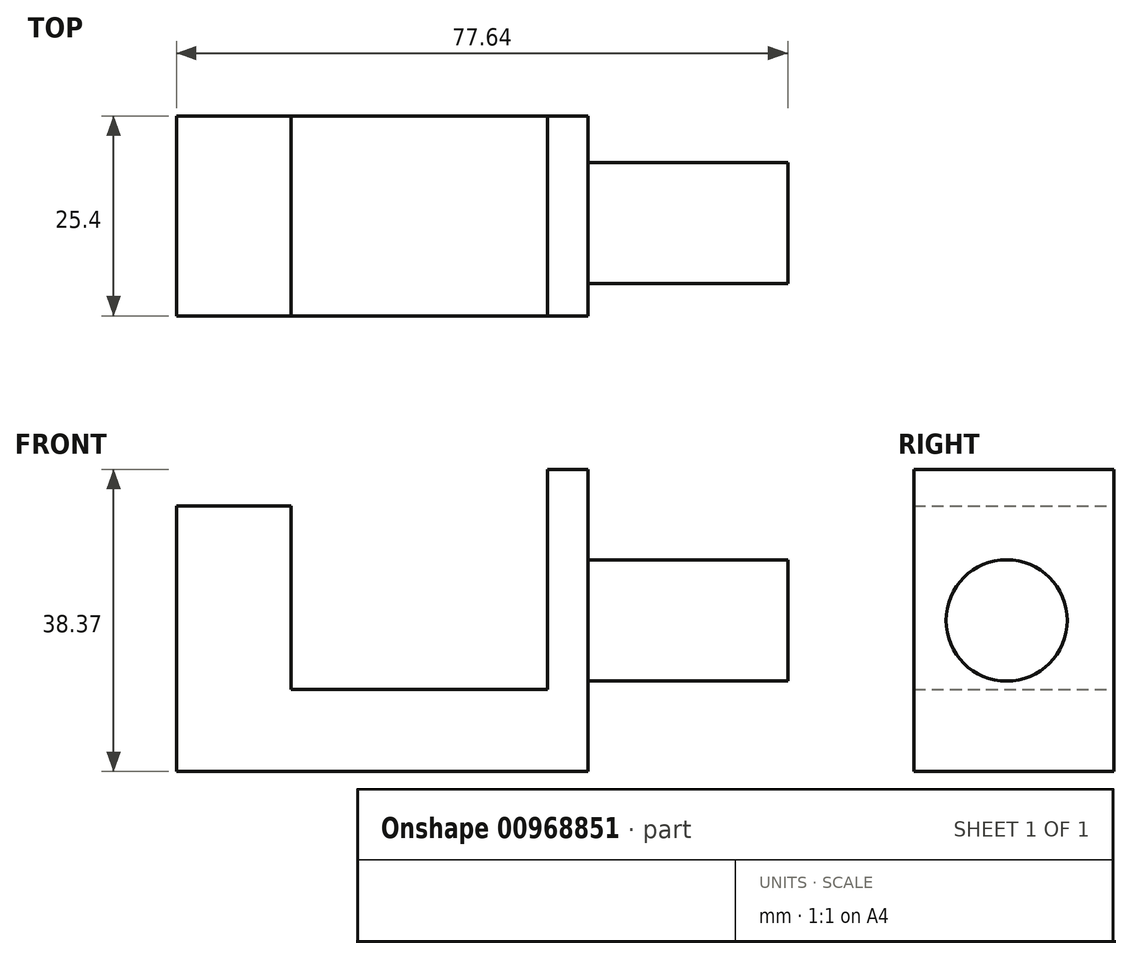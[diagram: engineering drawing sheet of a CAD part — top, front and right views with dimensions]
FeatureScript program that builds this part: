
annotation { "Feature Type Name" : "Feature", "Feature Type Description" : "" }
export const myFeature = defineFeature(function(context is Context, id is Id, definition is map)
    precondition{}
    {
        {
            var Q0;
            Q0=qCreatedBy(makeId("Front.planeOp"),FACE);
            var sketch = newSketch(context, id + "F0", { "sketchPlane" : qUnion([Q0])});
            skLineSegment(sketch, "E0", {"start": v(0, 0) * mm, "end": v(52.24, 0) * mm});
            skLineSegment(sketch, "E1", {"start": v(52.24, 0) * mm, "end": v(52.24, 38.37) * mm});
            skLineSegment(sketch, "E2", {"start": v(52.24, 38.37) * mm, "end": v(47.12, 38.37) * mm});
            skLineSegment(sketch, "E3", {"start": v(47.12, 38.37) * mm, "end": v(47.12, 10.43) * mm});
            skLineSegment(sketch, "E4", {"start": v(47.12, 10.43) * mm, "end": v(14.54, 10.43) * mm});
            skLineSegment(sketch, "E5", {"start": v(14.54, 10.43) * mm, "end": v(14.54, 33.74) * mm});
            skLineSegment(sketch, "E6", {"start": v(14.54, 33.74) * mm, "end": v(0, 33.74) * mm});
            skLineSegment(sketch, "E7", {"start": v(0, 33.74) * mm, "end": v(0, 0) * mm});
            skSolve(sketch);
        }
        {
            var Q0;
            Q0 = qSketchRegion(id + "F0", true);
            extrude(context, id + "F1", {"entities" : qUnion([Q0]), "depth" : 25.4 * mm, "offsetDistance" : 25.4 * mm});
        }
        {
            var Q0;
            Q0=makeQuery(id+"F1.opExtrude","SWEPT_FACE",FACE,{"disambiguationData":[OSD([sQuery(id+"F0.wireOp",EDGE,"E1")])]});
            var sketch = newSketch(context, id + "F2", { "sketchPlane" : qUnion([Q0])});
            skCircle(sketch, "E8", {"center": v(-13.6, 19.18) * mm, "radius": 7.7 * mm});
            skSolve(sketch);
        }
        {
            var Q0;
            Q0 = qSketchRegion(id + "F2", true);
            extrude(context, id + "F3", {"entities" : qUnion([Q0]), "operationType" : NewBodyOperationType.ADD, "depth" : 25.4 * mm, "offsetDistance" : 25.4 * mm});
        }
    });
